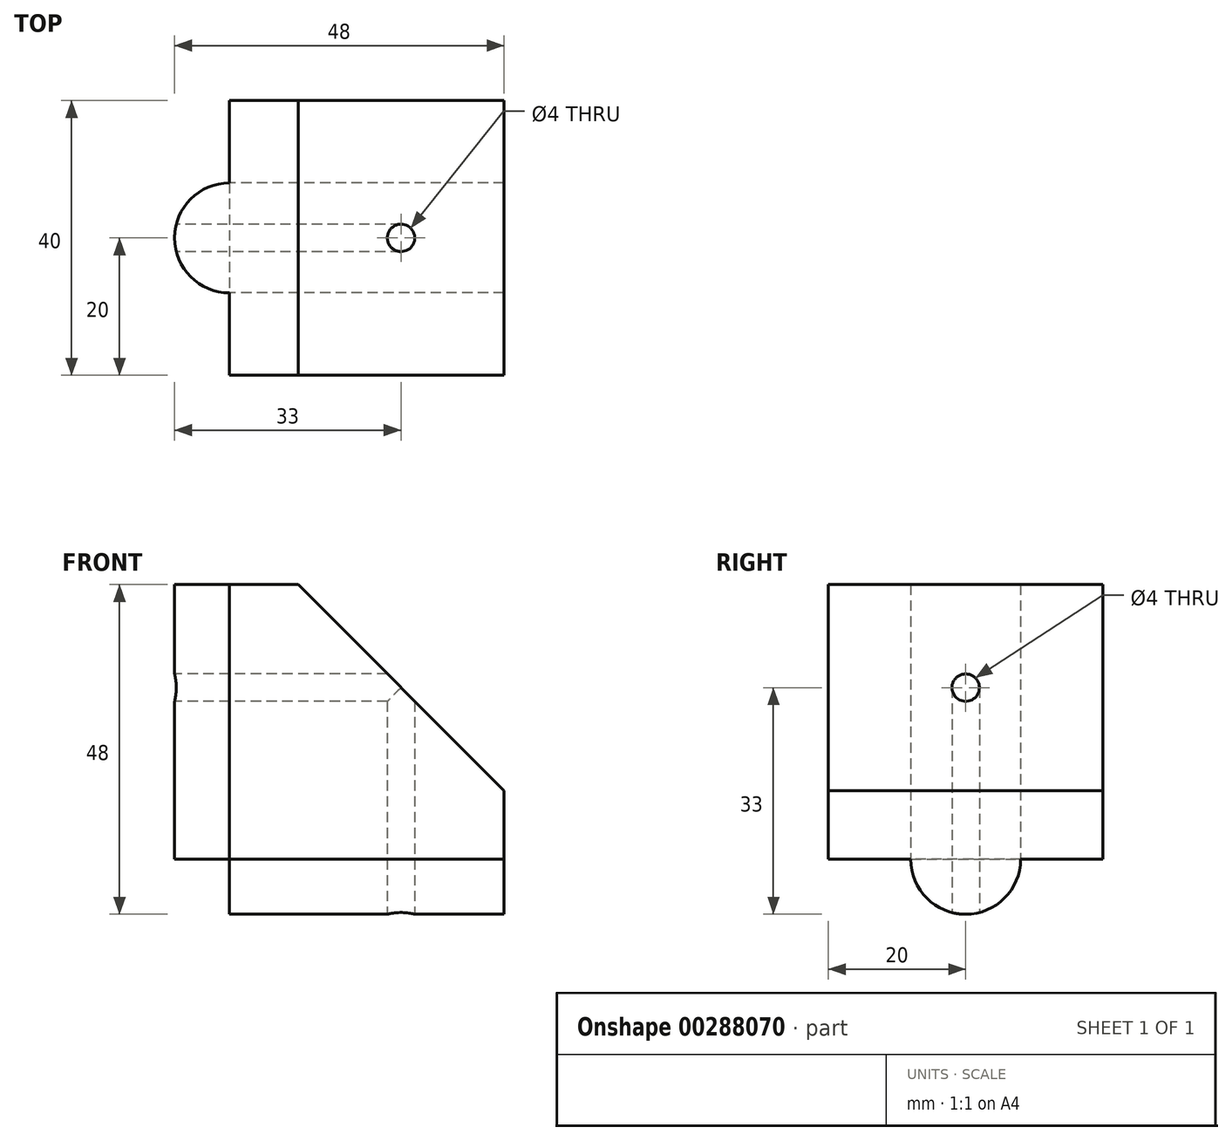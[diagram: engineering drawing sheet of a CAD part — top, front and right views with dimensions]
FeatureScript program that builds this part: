
annotation { "Feature Type Name" : "Feature", "Feature Type Description" : "" }
export const myFeature = defineFeature(function(context is Context, id is Id, definition is map)
    precondition{}
    {
        {
            var Q0;
            Q0=qCreatedBy(makeId("Front.planeOp"),FACE);
            var sketch = newSketch(context, id + "F0", { "sketchPlane" : qUnion([Q0])});
            skLineSegment(sketch, "E0", {"start": v(0, 0) * mm, "end": v(0, 40) * mm});
            skLineSegment(sketch, "E1", {"start": v(0, 40) * mm, "end": v(10, 40) * mm});
            skLineSegment(sketch, "E2", {"start": v(10, 40) * mm, "end": v(40, 10) * mm});
            skLineSegment(sketch, "E3", {"start": v(40, 10) * mm, "end": v(40, 0) * mm});
            skLineSegment(sketch, "E4", {"start": v(40, 0) * mm, "end": v(0, 0) * mm});
            skSolve(sketch);
        }
        {
            var Q0;
            Q0 = qSketchRegion(id + "F0", true);
            extrude(context, id + "F1", {"entities" : qUnion([Q0]), "endBound" : BoundingType.SYMMETRIC, "depth" : 40 * mm});
        }
        {
            var Q0;
            Q0=makeQuery(id+"F1.opExtrude","SWEPT_FACE",FACE,{"disambiguationData":[OSD([sQuery(id+"F0.wireOp",EDGE,"E0")])]});
            var sketch = newSketch(context, id + "F2", { "sketchPlane" : qUnion([Q0])});
            skCircle(sketch, "E5", {"center": v(0, 0) * mm, "radius": 8 * mm});
            skSolve(sketch);
        }
        {
            var Q0;
            {var subQ0=sQuery(id+"F2.wireOp",EDGE,"E5");var subQ1=makeQuery(id+"F1.opExtrude","SWEPT_EDGE",EDGE,{"disambiguationData":[OSD([sQuery(id+"F0.wireOp",EDGE,"E0"),sQuery(id+"F0.wireOp",EDGE,"E4")])]});var subQ2=makeQuery(id+"F2.imprint","INTERSECT",VERTEX,{"disambiguationData":[OD(0.0)],"derivedFrom":[subQ1,subQ0]});Q0=makeQuery(id+"F2.imprint","IMPRINT",FACE,{"disambiguationData":[TD([[makeQuery(id+"F2.imprint","IMPRINT",EDGE,{"disambiguationData":[TD([[subQ2,-1.0]])],"derivedFrom":subQ0}),1.0]])]});}
            extrude(context, id + "F3", {"entities" : qUnion([Q0]), "operationType" : NewBodyOperationType.ADD, "oppositeDirection" : true, "depth" : 40 * mm});
        }
        {
            var Q0;
            Q0=makeQuery(id+"F1.opExtrude","SWEPT_FACE",FACE,{"disambiguationData":[OSD([sQuery(id+"F0.wireOp",EDGE,"E4")])]});
            var sketch = newSketch(context, id + "F4", { "sketchPlane" : qUnion([Q0])});
            skCircle(sketch, "E6", {"center": v(0, 0) * mm, "radius": 8 * mm});
            skSolve(sketch);
        }
        {
            var Q0;
            {var subQ0=sQuery(id+"F4.wireOp",EDGE,"E6");var subQ1=makeQuery(id+"F1.opExtrude","SWEPT_EDGE",EDGE,{"disambiguationData":[OSD([sQuery(id+"F0.wireOp",EDGE,"E0"),sQuery(id+"F0.wireOp",EDGE,"E4")])]});var subQ2=makeQuery(id+"F4.imprint","INTERSECT",VERTEX,{"disambiguationData":[OD(0.0)],"derivedFrom":[subQ1,subQ0]});Q0=makeQuery(id+"F4.imprint","IMPRINT",FACE,{"disambiguationData":[TD([[makeQuery(id+"F4.imprint","IMPRINT",EDGE,{"disambiguationData":[TD([[subQ2,1.0]])],"derivedFrom":subQ0}),1.0]])]});}
            extrude(context, id + "F5", {"entities" : qUnion([Q0]), "operationType" : NewBodyOperationType.ADD, "oppositeDirection" : true, "depth" : 40 * mm});
        }
        {
            var Q0;
            Q0=makeQuery(id+"F1.opExtrude","SWEPT_FACE",FACE,{"disambiguationData":[OSD([sQuery(id+"F0.wireOp",EDGE,"E0")])]});
            var sketch = newSketch(context, id + "F6", { "sketchPlane" : qUnion([Q0])});
            skCircle(sketch, "E7", {"center": v(0, 25) * mm, "radius": 2 * mm});
            skSolve(sketch);
        }
        {
            var Q0;
            Q0 = qSketchRegion(id + "F6", true);
            extrude(context, id + "F7", {"entities" : qUnion([Q0]), "operationType" : NewBodyOperationType.REMOVE, "endBound" : BoundingType.SYMMETRIC, "oppositeDirection" : true, "depth" : 100 * mm});
        }
        {
            var Q0;
            Q0=makeQuery(id+"F1.opExtrude","SWEPT_FACE",FACE,{"disambiguationData":[OSD([sQuery(id+"F0.wireOp",EDGE,"E4")])]});
            var sketch = newSketch(context, id + "F8", { "sketchPlane" : qUnion([Q0])});
            skCircle(sketch, "E8", {"center": v(25, 0) * mm, "radius": 2 * mm});
            skSolve(sketch);
        }
        {
            var Q0;
            Q0 = qSketchRegion(id + "F8", true);
            extrude(context, id + "F9", {"entities" : qUnion([Q0]), "operationType" : NewBodyOperationType.REMOVE, "endBound" : BoundingType.SYMMETRIC, "oppositeDirection" : true, "depth" : 100 * mm});
        }
    });
